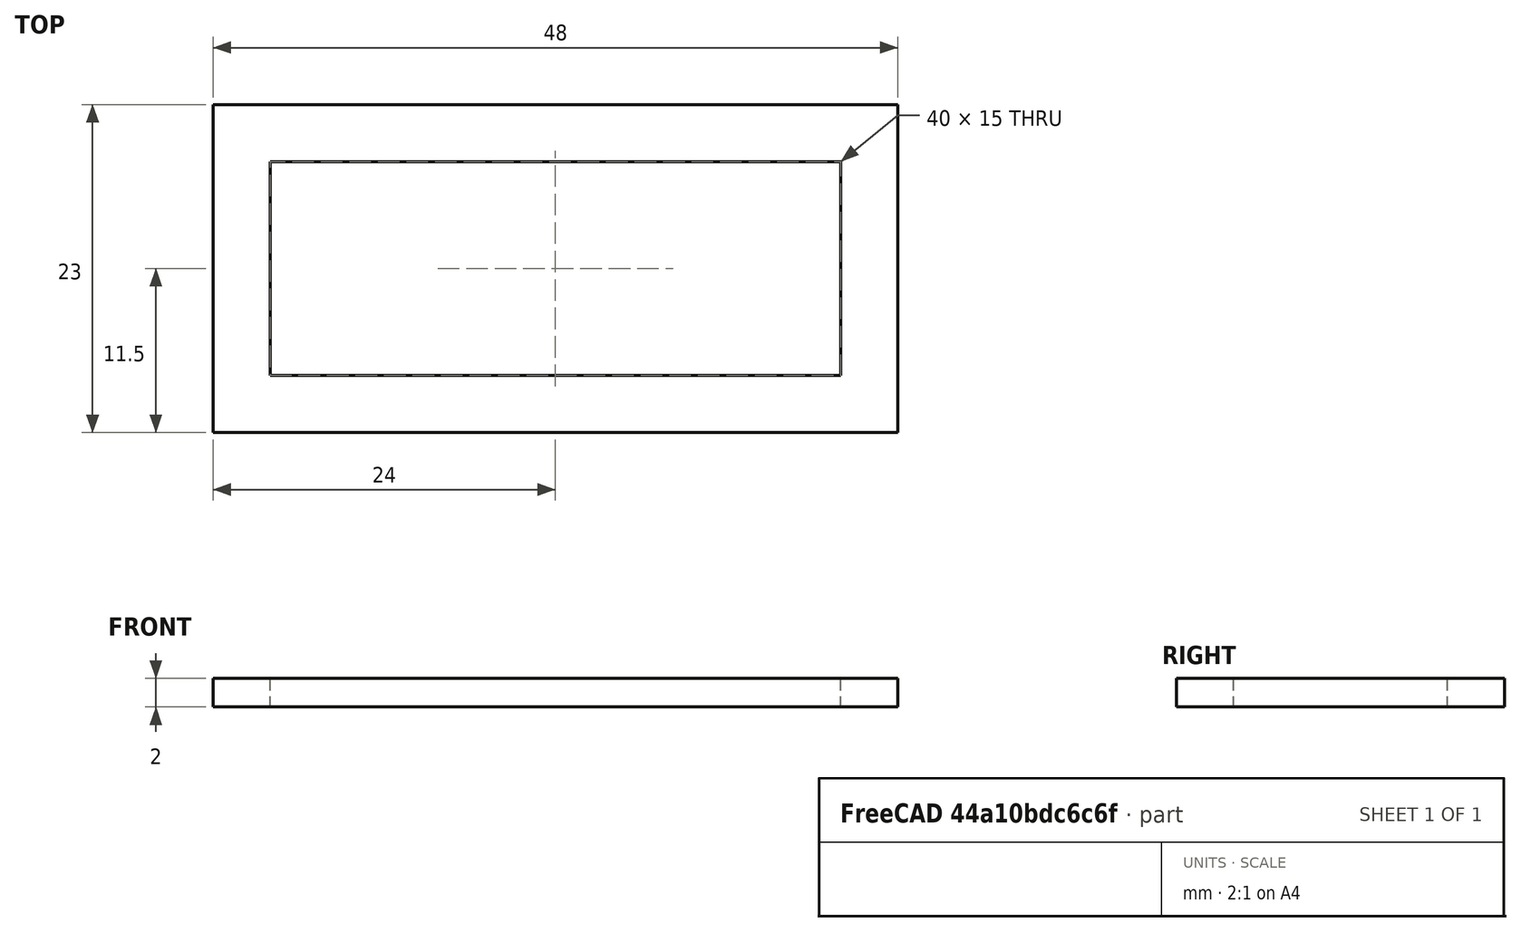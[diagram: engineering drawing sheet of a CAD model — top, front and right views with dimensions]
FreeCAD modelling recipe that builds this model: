
FCSTD DOCUMENT  (FreeCAD 0.16R6706 (Git))
Label: iROB-EA_ModuloPrincipal_Trasera_Marco
License: All rights reserved
LicenseURL: http://en.wikipedia.org/wiki/All_rights_reserved
objects: Sketcher::SketchObject×1, PartDesign::Pad×1
note: 3 computed .brp shape members not serialized (recipe doc carries the construction recipe); baked Part::Feature solids carry a one-line shape summary decoded from their .brp

FEATURE [Sketcher::SketchObject] Sketch  label="Marco"
  sketch-geometry (8):
    g0: LineSegment StartX=0 StartY=23 StartZ=0 EndX=48 EndY=23 EndZ=0
    g1: LineSegment StartX=48 StartY=23 StartZ=0 EndX=48 EndY=0 EndZ=0
    g2: LineSegment StartX=48 StartY=0 StartZ=0 EndX=0 EndY=0 EndZ=0
    g3: LineSegment StartX=0 StartY=0 StartZ=0 EndX=0 EndY=23 EndZ=0
    g4: LineSegment StartX=4 StartY=19 StartZ=0 EndX=44 EndY=19 EndZ=0
    g5: LineSegment StartX=44 StartY=19 StartZ=0 EndX=44 EndY=4 EndZ=0
    g6: LineSegment StartX=44 StartY=4 StartZ=0 EndX=4 EndY=4 EndZ=0
    g7: LineSegment StartX=4 StartY=4 StartZ=0 EndX=4 EndY=19 EndZ=0
  constraints (23):
    c: Coincident(g0,g1)
    c: Coincident(g1,g2)
    c: Coincident(g2,g3)
    c: Coincident(g3,g0)
    c: Horizontal(g0)
    c: Horizontal(g2)
    c: Vertical(g1)
    c: Vertical(g3)
    c: DistanceX(g0,g0) = 48
    c: DistanceY(g3,g3) = 23
    c: Coincident(g2,g-1)
    c: Coincident(g4,g5)
    c: Coincident(g5,g6)
    c: Coincident(g6,g7)
    c: Coincident(g7,g4)
    c: Horizontal(g4)
    c: Horizontal(g6)
    c: Vertical(g5)
    c: Vertical(g7)
    c: DistanceX(g4,g4) = 40
    c: DistanceY(g7,g7) = 15
    c: DistanceX(g-1,g6) = 4
    c: DistanceY(g6,g-1) = -4
FEATURE [PartDesign::Pad] Pad
  Length = 2
  Length2 = 100
  Sketch = -> Sketch
  Type = 0
